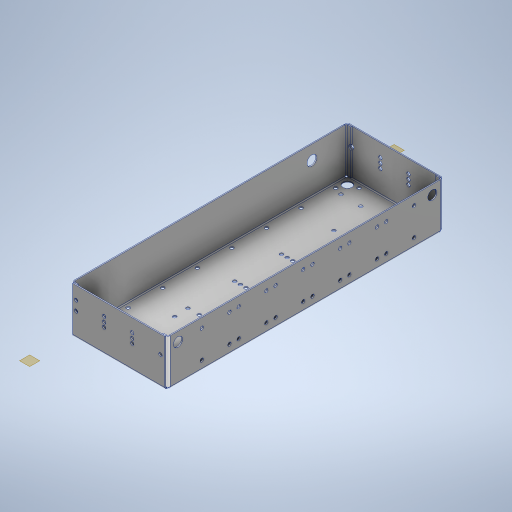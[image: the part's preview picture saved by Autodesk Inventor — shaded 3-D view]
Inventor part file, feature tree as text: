
AUTODESK INVENTOR PART (.ipt)
format: ipt  version: 2023 (Build 270158000, 158)  size: 707,072 bytes
history: native  units: in
note: dims shown in document units (in); Inventor stores cm internally (conversion verified against a paired STEP export)
features: sketch x22, hole x18, sheet_metal_op x12, pattern_linear x10, other x6, plane x4
ambient origin geometry x8: Origin, YZ Plane, XZ Plane, XY Plane, X Axis, Y Axis, Z Axis, Center Point
bodies: Solid1 (feature_tree)
feature tree (72):
  sheet_metal_op  "Face1"
  sheet_metal_op  "Flange1"
  sheet_metal_op  "Flange2"
  sheet_metal_op  "Unfold1"
  hole  "Hole1"  [1 undecoded]
  pattern_linear  "Rectangular Pattern1"  Count1=30  [1 undecoded]
  pattern_linear  "Rectangular Pattern2"  Count1=10  [1 undecoded]
  hole  "Hole2"  [1 undecoded]
  pattern_linear  "Rectangular Pattern3"  Count1=10 Spacing1=90.0deg
  hole  "Hole3"  [1 undecoded]
  hole  "Hole6"  [1 undecoded]
  pattern_linear  "Rectangular Pattern6"  Count1=10 Spacing1=90.0deg
  plane  "Work Plane4"
  hole  "Hole7"  [1 undecoded]
  plane  "Work Plane3"
  hole  "Hole8"  [1 undecoded]
  plane  "Work Plane2"
  hole  "Hole9"  [1 undecoded]
  plane  "Work Plane1"
  hole  "Hole10"  [1 undecoded]
  hole  "Hole11"  [1 undecoded]
  hole  "Hole12"  [1 undecoded]
  hole  "Hole13"  [1 undecoded]
  pattern_linear  "Rectangular Pattern11"  Count1=6  [1 undecoded]
  pattern_linear  "Rectangular Pattern12"  Count1=6  [1 undecoded]
  pattern_linear  "Rectangular Pattern13"  Count1=6  [1 undecoded]
  pattern_linear  "Rectangular Pattern14"  Count1=2  [1 undecoded]
  sheet_metal_op  "Refold6"
  sheet_metal_op  "Flange8"
  hole  "Hole14"  [1 undecoded]
  hole  "Hole15"  [1 undecoded]
  hole  "Hole16"  [1 undecoded]
  hole  "Hole17"  [1 undecoded]
  hole  "Hole18"  [1 undecoded]
  hole  "Hole19"  [1 undecoded]
  pattern_linear  "Rectangular Pattern15"  Spacing1=2.6949in  [1 undecoded]
  hole  "Hole20"  [1 undecoded]
  pattern_linear  "Rectangular Pattern16"  Spacing1=0.9626in  [1 undecoded]
  sketch  "Sketch1"  dims[d0=23.622in d1=7.874in d2=11.811in d3=3.937in]
  other  "Plate1"
  sketch  "Sketch2"  dims[d4=0.0875in d5=0.0875in]
  other  "Plate2"
  sheet_metal_op  "Bend1"
  sheet_metal_op  "Corner1"
  sketch  "Sketch3"  dims[d6=0.0438in]
  other  "Plate3"
  sheet_metal_op  "Bend2"
  sheet_metal_op  "Corner2"
  sketch  "Sketch5"  dims[d7=0.175in]
  sketch  "Sketch6"  dims[d8=0.0875in d9=3.937in d10=90.0deg d11=0.0787in]
  sketch  "Sketch7"  dims[d12=0.35in d13=0.0875in]
  sketch  "Sketch10"  dims[d14=0.0875in d15=0.0875in]
  sketch  "Sketch11"  dims[d16=0.0438in]
  sketch  "Sketch13"  dims[d17=0.175in]
  sketch  "Sketch15"  dims[d18=0.0875in d19=3.937in d20=90.0deg d21=0.0787in]
  sketch  "Sketch16"  dims[d22=0.35in d23=0.0875in]
  sketch  "Sketch17"  dims[d24=0.0875in]
  sketch  "Sketch21"  dims[d35=0.2969in d36=0.2953in d37=0.1476in d38=0.0984in d39=90.0deg d40=0.0875in d41=0.8108in]
  sketch  "Sketch25"  dims[d42=0.7874in d44=0.9646in d46=1.1811in d48=3.9921in]
  sketch  "Sketch26"  dims[d49=0.2969in d50=0.2953in d51=0.1476in d52=0.0984in d53=90.0deg d54=0.3937in d55=0.8108in d56=0.9646in]
  other  "Plate9"
  sheet_metal_op  "Bend8"
  sheet_metal_op  "Corner8"
  sketch  "Sketch27"  dims[d57=0.9646in d58=0.4823in]
  sketch  "Sketch28"  dims[d59=1.1811in d61=3.9921in]
  sketch  "Sketch29"  dims[d62=0.7874in d63=0.2953in d64=0.1476in d65=0.0984in d66=90.0deg d67=0.3937in d68=0.8108in d69=0.5906in]
  sketch  "Sketch30"  dims[d70=0.5906in]
  sketch  "Sketch31"  dims[d95=0.2969in d96=0.2953in d97=0.1476in d98=0.0984in d99=90.0deg d100=0.0875in d101=0.8108in d102=2.3622in d103=2.3622in d104=2.3622in d105=0.7874in]
  sketch  "Sketch32"  dims[d106=2.3622in d107=2.3622in d109=3.1496in]
  sketch  "Sketch33"  dims[d110=0.2969in d111=0.2953in d112=0.1476in d113=0.0984in d114=90.0deg d115=0.0875in d116=0.8108in d122=0.2969in d123=0.2953in d124=0.1476in d125=0.0984in d126=90.0deg d127=0.3937in d128=0.8108in d129=0.8071in d130=0.4035in d134=0.2969in d135=0.2953in d136=0.1476in d137=0.0984in d138=90.0deg d139=0.3937in d140=0.8108in d144=0.2969in d145=0.2953in d146=0.1476in d147=0.0984in d148=90.0deg d149=0.3937in d150=0.8108in d151=0.8071in d158=0.2969in d159=0.2953in d160=0.1476in d161=0.0984in d162=90.0deg d163=0.3937in d164=0.8108in d165=1.9252in d166=2.6949in d167=1.1811in d168=0.9626in d169=0.7874in d170=0.2953in d171=0.1476in d172=0.0984in d173=90.0deg d174=0.3937in d175=0.8108in d176=0.7874in d177=0.2953in d178=0.1476in d179=0.0984in d180=90.0deg d181=0.3937in d182=0.8108in d183=0.7874in d184=0.7874in d185=0.7874in d186=0.7874in d188=0.374in d189=2.433in d190=0.3346in d191=2.433in d192=1.1811in d194=2.4016in d195=1.1811in d197=2.4016in d198=1.1811in d200=2.4016in d201=1.1811in d203=2.4016in d205=7.0866in d206=0.5316in d231=0.0984in d250=0.0591in d263=0.0197in d265=0.0197in d271=0.0875in d272=0.0in d273=0.0875in d274=0.0in d275=0.0875in d276=0.0438in d277=0.175in d278=0.0875in d279=0.4921in d280=90.0deg d281=0.0984in d282=0.35in d283=0.0875in d284=0.0875in d285=7.874in d286=2.4016in d287=0.4331in d288=0.2953in d289=0.1476in d290=0.0984in d291=90.0deg d292=0.0875in d293=0.0in d294=0.4331in d295=0.2953in d296=0.1476in d297=0.0984in d298=90.0deg d299=0.3937in d300=0.0in d301=0.8386in d302=0.2953in d303=0.1476in d304=0.0984in d305=90.0deg d306=0.0875in d307=0.8108in d308=0.2969in d309=0.2953in d310=0.1476in d311=0.0984in d312=90.0deg d313=0.3937in d314=0.8108in d316=2.2441in d319=0.2969in d320=0.2953in d321=0.1476in d322=0.0984in d323=90.0deg d324=0.3937in d325=0.8108in d326=1.0236in d327=1.5748in d328=2.9528in d329=2.5591in d330=1.0236in d331=2.7559in d332=0.5906in d333=0.0591in d334=0.2969in d335=0.2953in d336=0.1476in d337=0.0984in d338=90.0deg d339=0.0875in d340=0.8108in d341=0.5in d342=1.5in d343=3.1496in d345=2.9528in d346=0.7874in d348=7.2065in d349=0.2969in d350=0.2953in d351=0.1476in d352=0.0984in d353=90.0deg d354=0.0875in d355=0.8108in d356=0.5in d357=1.5in d358=1.1811in d360=2.9528in d361=0.7874in d363=22.622in]
  other  "Cut4"
  other  "Cut5"
note: 26 required parameter values undecoded (feature->parameter linkage not recoverable at this tier; creation-order binding heuristic only, values carry confidence <= 0.55)
